# Revit family: Hager-Madrid-IP65-D200-Cl.I-Steel_encl-630A-NoHosted-IT-it
name_source: partatom
category: Electrical Equipment
units: mm (PartAtom-declared; Revit-internal decimal feet)

## family parameters
Always vertical = Yes
Cut with Voids When Loaded = No
Panel Configuration = Two Columns, Circuits Across
Part Type = Panelboard
Room Calculation Point = No
Round Connector Dimension = Use Diameter
Shared = No
Work Plane-Based = Yes

## types (12) — shared parameters
Default Elevation = 1219 mm
EF000003 - Tipo di montaggio = EV000384 - A parete
EF000007 - colore = EV000270 - grigio
EF000049 - profondità = 200 mm  [stored 0.656168 ft]
EF000116 - numero RAL = 7035
EF000118 - con piastra di montaggio = Yes
EF000339 - tipo di copertura = EV004216 - porta
EF001088 - possibilità di applicazione = Yes
EF001131 - profondità interna = 200 mm  [stored 0.656168 ft]
EF001596 - Attacco Lampada = EV000179 - acciaio
EF001613 - Integrità del circuito = EV000494 - senza
EF003532 - adatto per uso esterno = No
EF004293 - resistenza agli urti = EV008784 - IK10
EF004464 - tipo di porta = EV002646 - singolo
EF005474 - grado di protezione (IP) = EV006421 - IP65
EF007800 - adatto per parafulmine = No
EF008873 - corrente nominale (In) = 630 A
EF009170 - spessore materiale scatola = 1 mm  [stored 0.00328084 ft]
EF009171 - spessore materiale porta/coperchio = 2 mm  [stored 0.00656168 ft]
EF009212 - esecuzione coperchio = EV000116 - chiuso
EF015940 - Coprire con rilascio di sovrapressione = No
HG000002 - Con porta = Yes
HG000003 - Gamma = Madrid
HG000006 - Ad incasso = No
HG000009 - Porta doppia a battente = No
HG000010 - Porte asimmetriche = No
HG000023 - Custodia a doppia sezione = No
HG000024 - Altezza della sezione inferiore = 600 mm
HG000026 - A pavimento = No
Manufacturer = Hager
Type Comments = Madrid
zero-valued in all types: EF000218 - profondità di incasso, EF002950 - Numero moduli DIN, EF004427 - numero di moduli, HG000027 - Altezza dello zoccolo

## per-type parameters (varying)
| type | EF000008 - Larghezza | EF000040 - Altezza | EF000266 - numero di file | EF000437 - numero di ingressi per conduttori | EF006244 - coperchio/porta trasparente | EF006306 - con serratura | EF009554 - numero delle aperture per la piastra della flangia | HG000004 - Codice produttore |
| A parete IP65 L300 A400 P200  - 35707 | 300 mm | 400 mm  [stored 1.31234 ft] | 0 | 2 | No | Yes | 2 | 35707 |
| A parete IP65 L300 A400 P200  - 35757 | 300 mm | 400 mm  [stored 1.31234 ft] | 0 | 2 | Yes | No | 2 | 35757 |
| A parete IP65 L400 A400 P200  - 35708 | 400 mm  [stored 1.31234 ft] | 400 mm  [stored 1.31234 ft] | 0 | 2 | No | Yes | 2 | 35708 |
| A parete IP65 L400 A400 P200  - 35758 | 400 mm  [stored 1.31234 ft] | 400 mm  [stored 1.31234 ft] | 0 | 2 | Yes | No | 2 | 35758 |
| A parete IP65 L400 A500 P200  - 35713 | 400 mm  [stored 1.31234 ft] | 500 mm  [stored 1.64042 ft] | 1 | 2 | No | Yes | 2 | 35713 |
| A parete IP65 L400 A500 P200  - 35763 | 400 mm  [stored 1.31234 ft] | 500 mm  [stored 1.64042 ft] | 3 | 2 | Yes | No | 2 | 35763 |
| A parete IP65 L400 A600 P200  - 35714 | 400 mm  [stored 1.31234 ft] | 600 mm | 0 | 2 | No | Yes | 2 | 35714 |
| A parete IP65 L400 A600 P200  - 35764 | 400 mm  [stored 1.31234 ft] | 600 mm | 0 | 2 | Yes | No | 2 | 35764 |
| A parete IP65 L500 A500 P200  - 35716 | 500 mm  [stored 1.64042 ft] | 500 mm  [stored 1.64042 ft] | 0 | 2 | No | Yes | 2 | 35716 |
| A parete IP65 L500 A500 P200  - 35766 | 500 mm  [stored 1.64042 ft] | 500 mm  [stored 1.64042 ft] | 0 | 2 | Yes | No | 2 | 35766 |
| A parete IP65 L500 A650 P200  - 35720 | 500 mm  [stored 1.64042 ft] | 650 mm  [stored 2.13255 ft] | 1 | 0 | No | Yes | 0 | 35720 |
| A parete IP65 L500 A650 P200  - 35770 | 500 mm  [stored 1.64042 ft] | 650 mm  [stored 2.13255 ft] | 4 | 2 | Yes | No | 2 | 35770 |

note: [stored X ft] marks values corroborated as IEEE doubles in the binary element streams (Revit-internal decimal feet)

## geometry (parser evidence)
native form markers: Blend x4, Sweep x9
no freeform markers — native parametric forms only
